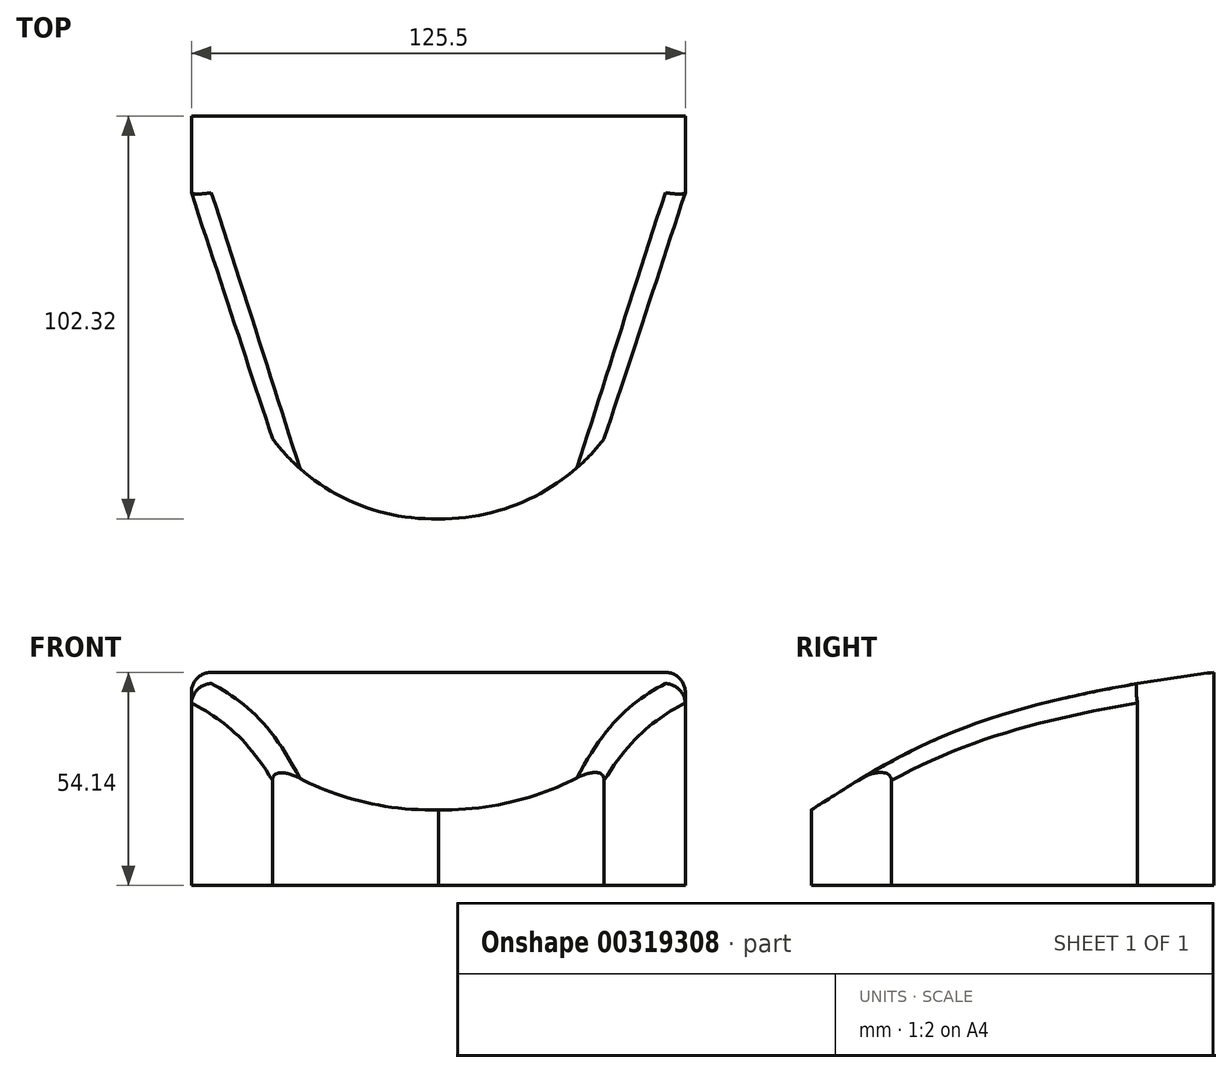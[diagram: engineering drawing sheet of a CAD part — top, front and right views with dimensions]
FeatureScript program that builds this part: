
annotation { "Feature Type Name" : "Feature", "Feature Type Description" : "" }
export const myFeature = defineFeature(function(context is Context, id is Id, definition is map)
    precondition{}
    {
        {
            var Q0;
            Q0=qCreatedBy(makeId("Top.planeOp"),FACE);
            var sketch = newSketch(context, id + "F0", { "sketchPlane" : qUnion([Q0])});
            skLineSegment(sketch, "E0.bottom", {"start": v(-43.04, 40.75) * mm, "end": v(41.25, 40.75) * mm});
            skLineSegment(sketch, "E0.top", {"start": v(-43.04, -21.77) * mm, "end": v(41.25, -21.77) * mm});
            skLineSegment(sketch, "E0.left", {"start": v(-43.04, 40.75) * mm, "end": v(-43.04, -21.77) * mm});
            skLineSegment(sketch, "E0.right", {"start": v(41.25, 40.75) * mm, "end": v(41.25, -21.77) * mm});
            skLineSegment(sketch, "E1", {"start": v(41.25, -21.77) * mm, "end": v(61.86, 40.75) * mm});
            skLineSegment(sketch, "E2", {"start": v(61.86, 40.75) * mm, "end": v(41.25, 40.75) * mm});
            skLineSegment(sketch, "E3", {"start": v(-43.04, 40.75) * mm, "end": v(-63.64, 40.75) * mm});
            skLineSegment(sketch, "E4", {"start": v(-63.64, 40.75) * mm, "end": v(-43.04, -21.77) * mm});
            skLineSegment(sketch, "E5", {"start": v(-43.04, -21.77) * mm, "end": v(-0.9, -21.77) * mm, "construction": true});
            skArc(sketch, "E6", {"start": v(-43.04, -21.77) * mm, "mid": v(-24.44, -37.08) * mm, "end": v(-0.9, -42.11) * mm});
            skArc(sketch, "E7", {"start": v(-0.9, -42.11) * mm, "mid": v(22.58, -36.92) * mm, "end": v(41.25, -21.77) * mm});
            skSolve(sketch);
        }
        {
            var Q0;
            Q0=makeQuery(id+"F0.imprint","IMPRINT",FACE,{"disambiguationData":[TD([[makeQuery(id+"F0.imprint","IMPRINT",EDGE,{"derivedFrom":sQuery(id+"F0.wireOp",EDGE,"E0.bottom")}),-1.0]])]});
            var Q1;
            Q1=makeQuery(id+"F0.imprint","IMPRINT",FACE,{"disambiguationData":[TD([[makeQuery(id+"F0.imprint","IMPRINT",EDGE,{"derivedFrom":sQuery(id+"F0.wireOp",EDGE,"E0.right")}),1.0]])]});
            var Q2;
            Q2=makeQuery(id+"F0.imprint","IMPRINT",FACE,{"disambiguationData":[TD([[makeQuery(id+"F0.imprint","IMPRINT",EDGE,{"derivedFrom":sQuery(id+"F0.wireOp",EDGE,"E0.left")}),-1.0]])]});
            var Q3;
            Q3=makeQuery(id+"F0.imprint","IMPRINT",FACE,{"disambiguationData":[TD([[makeQuery(id+"F0.imprint","IMPRINT",EDGE,{"derivedFrom":sQuery(id+"F0.wireOp",EDGE,"E0.top")}),-1.0]])]});
            extrude(context, id + "F1", {"entities" : qUnion([Q0, Q1, Q2, Q3]), "depth" : 38.1 * mm});
        }
        {
            var Q0;
            Q0=makeQuery(id+"F1.opExtrude","SWEPT_FACE",FACE,{"disambiguationData":[OSD([sQuery(id+"F0.wireOp",EDGE,"E0.bottom"),sQuery(id+"F0.wireOp",EDGE,"E2"),sQuery(id+"F0.wireOp",EDGE,"E3")])]});
            extrude(context, id + "F2", {"entities" : qUnion([Q0]), "operationType" : NewBodyOperationType.ADD, "depth" : 19.43 * mm});
        }
        {
            var Q0;
            Q0=qCreatedBy(makeId("Right.planeOp"),FACE);
            var sketch = newSketch(context, id + "F3", { "sketchPlane" : qUnion([Q0])});
            skFitSpline(sketch, "E8", {"points": [v(-42.4, 38.06) * mm, v(0, 60.3) * mm, v(82.47, 75.43) * mm, v(150.18, 76.8) * mm], "startDerivative": vector(131.47, 84.73) * mm, "endDerivative": vector(190.03, -2.44) * mm});
            skLineSegment(sketch, "E9", {"start": v(-42.4, 38.06) * mm, "end": v(150.18, 38.06) * mm});
            skLineSegment(sketch, "E10", {"start": v(150.18, 38.06) * mm, "end": v(150.18, 76.8) * mm});
            skSolve(sketch);
        }
        {
            var Q0;
            Q0 = qSketchRegion(id + "F3", true);
            var Q1;
            Q1=makeQuery(id+"F3.imprint","IMPRINT",FACE,{"disambiguationData":[TD([[makeQuery(id+"F3.imprint","IMPRINT",EDGE,{"derivedFrom":sQuery(id+"F3.wireOp",EDGE,"E8")}),-1.0]])]});
            extrude(context, id + "F4", {"entities" : qUnion([Q0, Q1]), "operationType" : NewBodyOperationType.ADD, "endBound" : BoundingType.SYMMETRIC, "depth" : 152.4 * mm});
        }
        {
            var Q0;
            Q0=makeQuery(id+"F4.opExtrude","SWEPT_FACE",FACE,{"disambiguationData":[OSD([sQuery(id+"F3.wireOp",EDGE,"E9")])]});
            extrude(context, id + "F5", {"entities" : qUnion([Q0]), "operationType" : NewBodyOperationType.REMOVE, "oppositeDirection" : true, "depth" : 50.8 * mm});
        }
        {
            var Q0;
            {var subQ0=sQuery(id+"F0.wireOp",EDGE,"E3");var subQ1=sQuery(id+"F0.wireOp",EDGE,"E2");var subQ2=sQuery(id+"F0.wireOp",EDGE,"E0.bottom");Q0=makeQuery(id+"F2.boolean.opBoolean","MERGE",FACE,{"derivedFrom":[makeQuery(id+"F1.opExtrude","CAP_FACE",FACE,{"disambiguationData":[OSD([subQ2,sQuery(id+"F0.wireOp",EDGE,"E1"),subQ1,subQ0,sQuery(id+"F0.wireOp",EDGE,"E4"),sQuery(id+"F0.wireOp",EDGE,"E6"),sQuery(id+"F0.wireOp",EDGE,"E7")])],"isStart":true}),makeQuery(id+"F2.opExtrude","SWEPT_FACE",FACE,{"disambiguationData":[OSD([subQ2,subQ1,subQ0]),TDD([makeQuery(id+"F1.opExtrude","CAP_EDGE",EDGE,{"disambiguationData":[OSD([subQ2,subQ1,subQ0])],"isStart":true})])]})]});}
            extrude(context, id + "F6", {"entities" : qUnion([Q0]), "operationType" : NewBodyOperationType.REMOVE, "oppositeDirection" : true, "depth" : 19.05 * mm});
        }
        {
            var Q0;
            Q0=makeQuery(id+"F6.boolean.opBoolean","COPY",EDGE,{"derivedFrom":makeQuery(id+"F6.opExtrude","CAP_EDGE",EDGE,{"disambiguationData":[OSD([sQuery(id+"F0.wireOp",EDGE,"E3"),sQuery(id+"F0.wireOp",EDGE,"E4")])],"isStart":false})});
            var Q1;
            Q1=makeQuery(id+"F6.boolean.opBoolean","COPY",EDGE,{"derivedFrom":makeQuery(id+"F6.opExtrude","CAP_EDGE",EDGE,{"disambiguationData":[OSD([sQuery(id+"F0.wireOp",EDGE,"E4")])],"isStart":false})});
            var Q2;
            Q2=makeQuery(id+"F6.boolean.opBoolean","COPY",EDGE,{"derivedFrom":makeQuery(id+"F6.opExtrude","CAP_EDGE",EDGE,{"disambiguationData":[OSD([sQuery(id+"F0.wireOp",EDGE,"E1")])],"isStart":false})});
            var Q3;
            Q3=makeQuery(id+"F6.boolean.opBoolean","COPY",EDGE,{"derivedFrom":makeQuery(id+"F6.opExtrude","CAP_EDGE",EDGE,{"disambiguationData":[OSD([sQuery(id+"F0.wireOp",EDGE,"E1"),sQuery(id+"F0.wireOp",EDGE,"E2")])],"isStart":false})});
            var Q4;
            Q4=makeQuery(id+"F5.boolean.opBoolean","INTERSECT",EDGE,{"derivedFrom":[makeQuery(id+"F4.opExtrude","SWEPT_FACE",FACE,{"disambiguationData":[OSD([sQuery(id+"F3.wireOp",EDGE,"E8")])]}),makeQuery(id+"F5.opExtrude","SWEPT_FACE",FACE,{"disambiguationData":[OSD([sQuery(id+"F0.wireOp",EDGE,"E4"),sQuery(id+"F3.wireOp",EDGE,"E9")])]})]});
            var Q5;
            Q5=makeQuery(id+"F5.boolean.opBoolean","INTERSECT",EDGE,{"derivedFrom":[makeQuery(id+"F4.opExtrude","SWEPT_FACE",FACE,{"disambiguationData":[OSD([sQuery(id+"F3.wireOp",EDGE,"E8")])]}),makeQuery(id+"F5.opExtrude","SWEPT_FACE",FACE,{"disambiguationData":[OSD([sQuery(id+"F0.wireOp",EDGE,"E1"),sQuery(id+"F3.wireOp",EDGE,"E9")])]})]});
            var Q6;
            Q6=makeQuery(id+"F5.boolean.opBoolean","INTERSECT",EDGE,{"derivedFrom":[makeQuery(id+"F4.opExtrude","SWEPT_FACE",FACE,{"disambiguationData":[OSD([sQuery(id+"F3.wireOp",EDGE,"E8")])]}),makeQuery(id+"F5.opExtrude","SWEPT_FACE",FACE,{"disambiguationData":[OSD([sQuery(id+"F0.wireOp",EDGE,"E3"),sQuery(id+"F0.wireOp",EDGE,"E4"),sQuery(id+"F3.wireOp",EDGE,"E9")])]})]});
            var Q7;
            Q7=makeQuery(id+"F5.boolean.opBoolean","INTERSECT",EDGE,{"derivedFrom":[makeQuery(id+"F4.opExtrude","SWEPT_FACE",FACE,{"disambiguationData":[OSD([sQuery(id+"F3.wireOp",EDGE,"E8")])]}),makeQuery(id+"F5.opExtrude","SWEPT_FACE",FACE,{"disambiguationData":[OSD([sQuery(id+"F0.wireOp",EDGE,"E1"),sQuery(id+"F0.wireOp",EDGE,"E2"),sQuery(id+"F3.wireOp",EDGE,"E9")])]})]});
            fillet(context, id + "F7", {"entities" : qUnion([Q0, Q1, Q2, Q3, Q4, Q5, Q6, Q7]), "radius" : 5.08 * mm, "tangentPropagation" : true, "allowEdgeOverflow" : false});
        }
    });
